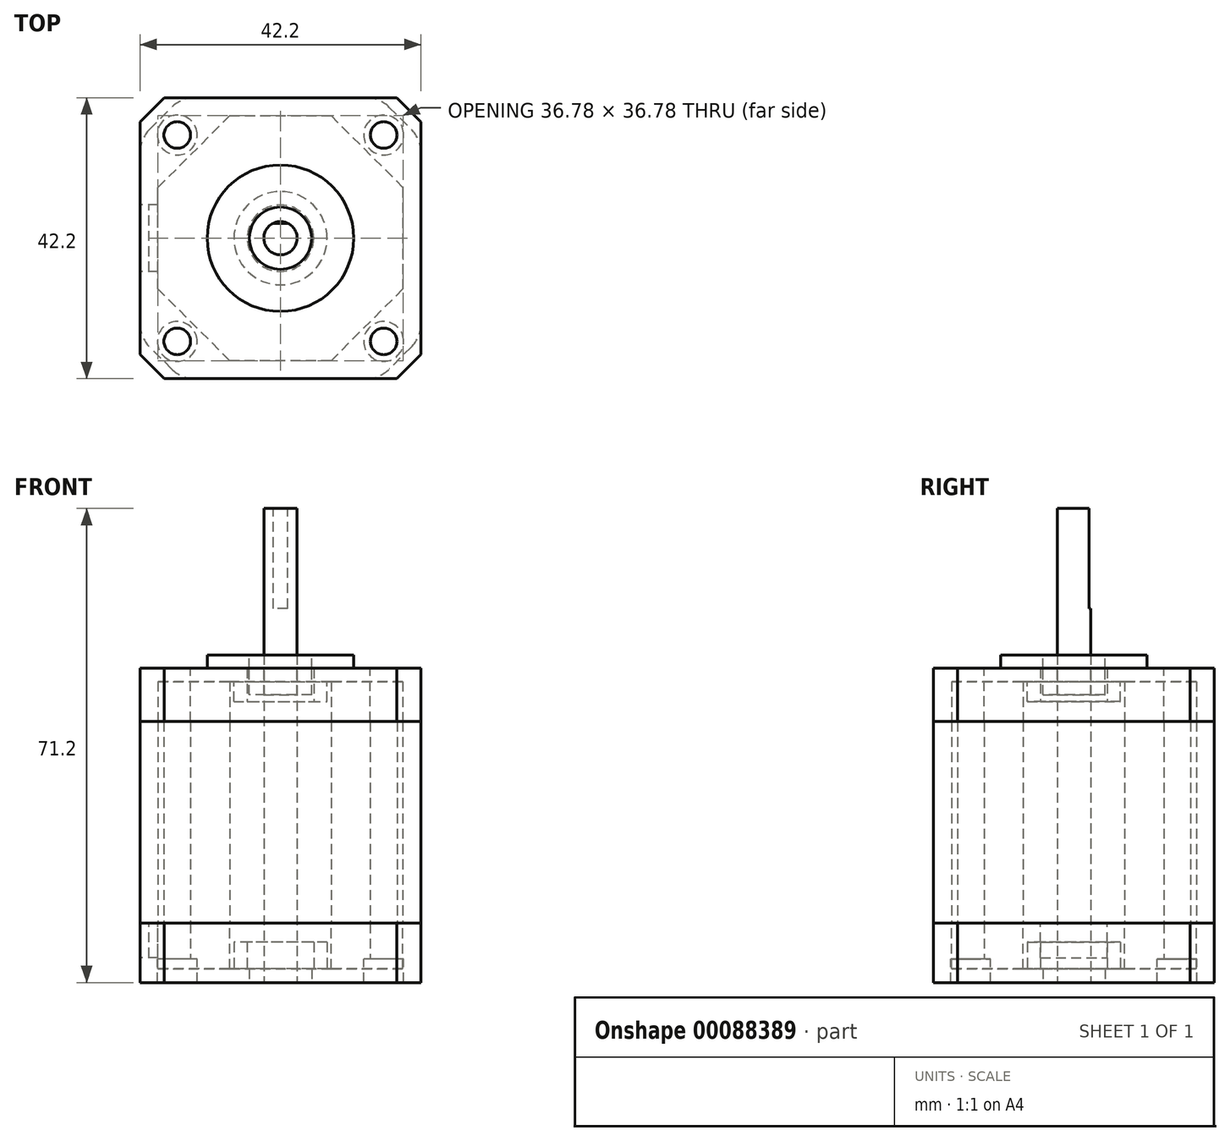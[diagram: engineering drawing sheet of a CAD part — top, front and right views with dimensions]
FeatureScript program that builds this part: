
annotation { "Feature Type Name" : "Feature", "Feature Type Description" : "" }
export const myFeature = defineFeature(function(context is Context, id is Id, definition is map)
    precondition{}
    {
        {
            var Q0;
            Q0=qCreatedBy(makeId("Top.planeOp"),FACE);
            var sketch = newSketch(context, id + "F0", { "sketchPlane" : qUnion([Q0])});
            skLineSegment(sketch, "E0.bottom", {"start": v(17.44, 21.1) * mm, "end": v(-17.44, 21.1) * mm});
            skLineSegment(sketch, "E0.top", {"start": v(17.44, -21.1) * mm, "end": v(-17.44, -21.1) * mm});
            skLineSegment(sketch, "E0.left", {"start": v(21.1, 17.44) * mm, "end": v(21.1, -17.44) * mm});
            skLineSegment(sketch, "E0.right", {"start": v(-21.1, 17.44) * mm, "end": v(-21.1, -17.44) * mm});
            skPoint(sketch, "E0.middle", {"position": v(0, 0) * mm});
            skLineSegment(sketch, "E1.bottom", {"start": v(15.5, 15.5) * mm, "end": v(-15.5, 15.5) * mm, "construction": true});
            skLineSegment(sketch, "E1.top", {"start": v(15.5, -15.5) * mm, "end": v(-15.5, -15.5) * mm, "construction": true});
            skLineSegment(sketch, "E1.left", {"start": v(15.5, 15.5) * mm, "end": v(15.5, -15.5) * mm, "construction": true});
            skLineSegment(sketch, "E1.right", {"start": v(-15.5, 15.5) * mm, "end": v(-15.5, -15.5) * mm, "construction": true});
            skCircle(sketch, "E2", {"center": v(-15.5, 15.5) * mm, "radius": 2 * mm});
            skCircle(sketch, "E3", {"center": v(15.5, 15.5) * mm, "radius": 2 * mm});
            skCircle(sketch, "E4", {"center": v(-15.5, -15.5) * mm, "radius": 2 * mm});
            skCircle(sketch, "E5", {"center": v(15.5, -15.5) * mm, "radius": 2 * mm});
            skLineSegment(sketch, "E6.1", {"start": v(-21.1, 17.44) * mm, "end": v(-17.44, 21.1) * mm});
            skLineSegment(sketch, "E7", {"start": v(0, 21.1) * mm, "end": v(0, -21.1) * mm, "construction": true});
            skLineSegment(sketch, "E8", {"start": v(-21.1, 0) * mm, "end": v(21.1, 0) * mm, "construction": true});
            skLineSegment(sketch, "E9.MirrorCS", {"start": v(21.1, 17.44) * mm, "end": v(17.44, 21.1) * mm});
            skLineSegment(sketch, "E10.MirrorCS", {"start": v(-21.1, -17.44) * mm, "end": v(-17.44, -21.1) * mm});
            skLineSegment(sketch, "E11.MirrorCS", {"start": v(21.1, -17.44) * mm, "end": v(17.44, -21.1) * mm});
            skCircle(sketch, "E12", {"center": v(0, 0) * mm, "radius": 4.68 * mm});
            skCircle(sketch, "E13", {"center": v(0, 0) * mm, "radius": 2.5 * mm});
            skCircle(sketch, "E14", {"center": v(0, 0) * mm, "radius": 11 * mm});
            skSolve(sketch);
        }
        {
            var Q0;
            Q0=makeQuery(id+"F0.imprint","IMPRINT",FACE,{"disambiguationData":[TD([[makeQuery(id+"F0.imprint","IMPRINT",EDGE,{"derivedFrom":sQuery(id+"F0.wireOp",EDGE,"E0.bottom")}),1.0]])]});
            var Q1;
            Q1=makeQuery(id+"F0.imprint","IMPRINT",FACE,{"disambiguationData":[TD([[makeQuery(id+"F0.imprint","IMPRINT",EDGE,{"derivedFrom":sQuery(id+"F0.wireOp",EDGE,"E12")}),-1.0]])]});
            extrude(context, id + "F1", {"entities" : qUnion([Q0, Q1]), "oppositeDirection" : true, "depth" : 8 * mm});
        }
        {
            var Q0;
            Q0=makeQuery(id+"F0.imprint","IMPRINT",FACE,{"disambiguationData":[TD([[makeQuery(id+"F0.imprint","IMPRINT",EDGE,{"derivedFrom":sQuery(id+"F0.wireOp",EDGE,"E12")}),-1.0]])]});
            extrude(context, id + "F2", {"entities" : qUnion([Q0]), "operationType" : NewBodyOperationType.ADD, "depth" : 2 * mm});
        }
        {
            var Q0;
            Q0=makeQuery(id+"F1.opExtrude","CAP_FACE",FACE,{"disambiguationData":[OSD([sQuery(id+"F0.wireOp",EDGE,"E0.bottom"),sQuery(id+"F0.wireOp",EDGE,"E0.top"),sQuery(id+"F0.wireOp",EDGE,"E0.left"),sQuery(id+"F0.wireOp",EDGE,"E0.right"),sQuery(id+"F0.wireOp",EDGE,"E2"),sQuery(id+"F0.wireOp",EDGE,"E3"),sQuery(id+"F0.wireOp",EDGE,"E4"),sQuery(id+"F0.wireOp",EDGE,"E5"),sQuery(id+"F0.wireOp",EDGE,"E6.1"),sQuery(id+"F0.wireOp",EDGE,"E9.MirrorCS"),sQuery(id+"F0.wireOp",EDGE,"E10.MirrorCS"),sQuery(id+"F0.wireOp",EDGE,"E11.MirrorCS"),sQuery(id+"F0.wireOp",EDGE,"E12")])],"isStart":true});
            cPlane(context, id + "F3", {"entities" : qUnion([Q0]), "cplaneType" : CPlaneType.OFFSET, "offset" : (47.2 - 3.5) * mm, "oppositeDirection" : true, "width" : 150 * mm, "height" : 150 * mm});
        }
        {
            var Q0;
            Q0=qCreatedBy(id+"F3.planeOp",FACE);
            var sketch = newSketch(context, id + "F4", { "sketchPlane" : qUnion([Q0])});
            skLineSegment(sketch, "E15.0", {"start": v(17.44, 21.1) * mm, "end": v(-17.44, 21.1) * mm});
            skLineSegment(sketch, "E15.1", {"start": v(17.44, -21.1) * mm, "end": v(-17.44, -21.1) * mm});
            skLineSegment(sketch, "E15.2", {"start": v(21.1, 17.44) * mm, "end": v(21.1, -17.44) * mm});
            skLineSegment(sketch, "E15.3", {"start": v(-21.1, 17.44) * mm, "end": v(-21.1, -17.44) * mm});
            skPoint(sketch, "E15.4", {"position": v(0, 0) * mm});
            skLineSegment(sketch, "E15.5", {"start": v(15.5, 15.5) * mm, "end": v(-15.5, 15.5) * mm, "construction": true});
            skLineSegment(sketch, "E15.6", {"start": v(15.5, -15.5) * mm, "end": v(-15.5, -15.5) * mm, "construction": true});
            skLineSegment(sketch, "E15.7", {"start": v(15.5, 15.5) * mm, "end": v(15.5, -15.5) * mm, "construction": true});
            skLineSegment(sketch, "E15.8", {"start": v(-15.5, 15.5) * mm, "end": v(-15.5, -15.5) * mm, "construction": true});
            skPoint(sketch, "E15.9", {"position": v(0, 0) * mm});
            skCircle(sketch, "E15.10", {"center": v(-15.5, 15.5) * mm, "radius": 2 * mm});
            skCircle(sketch, "E15.11", {"center": v(15.5, 15.5) * mm, "radius": 2 * mm});
            skCircle(sketch, "E15.12", {"center": v(-15.5, -15.5) * mm, "radius": 2 * mm});
            skCircle(sketch, "E15.13", {"center": v(15.5, -15.5) * mm, "radius": 2 * mm});
            skLineSegment(sketch, "E15.14", {"start": v(-21.1, 17.44) * mm, "end": v(-17.44, 21.1) * mm});
            skLineSegment(sketch, "E15.15", {"start": v(0, 21.1) * mm, "end": v(0, -21.1) * mm, "construction": true});
            skLineSegment(sketch, "E15.16", {"start": v(-21.1, 0) * mm, "end": v(21.1, 0) * mm, "construction": true});
            skLineSegment(sketch, "E15.17", {"start": v(21.1, 17.44) * mm, "end": v(17.44, 21.1) * mm});
            skLineSegment(sketch, "E15.18", {"start": v(-21.1, -17.44) * mm, "end": v(-17.44, -21.1) * mm});
            skLineSegment(sketch, "E15.19", {"start": v(21.1, -17.44) * mm, "end": v(17.44, -21.1) * mm});
            skCircle(sketch, "E15.20", {"center": v(0, 0) * mm, "radius": 4.68 * mm});
            skCircle(sketch, "E15.21", {"center": v(0, 0) * mm, "radius": 2.5 * mm});
            skCircle(sketch, "E16", {"center": v(15.5, 15.5) * mm, "radius": 3 * mm});
            skCircle(sketch, "E17.MirrorC", {"center": v(-15.5, 15.5) * mm, "radius": 3 * mm});
            skCircle(sketch, "E18.MirrorC", {"center": v(-15.5, -15.5) * mm, "radius": 3 * mm});
            skCircle(sketch, "E19.MirrorC", {"center": v(15.5, -15.5) * mm, "radius": 3 * mm});
            skSolve(sketch);
        }
        {
            var Q0;
            Q0=makeQuery(id+"F4.imprint","IMPRINT",FACE,{"disambiguationData":[TD([[makeQuery(id+"F4.imprint","IMPRINT",EDGE,{"derivedFrom":sQuery(id+"F4.wireOp",EDGE,"E15.0")}),1.0]])]});
            var Q1;
            Q1=makeQuery(id+"F4.imprint","IMPRINT",FACE,{"disambiguationData":[TD([[makeQuery(id+"F4.imprint","IMPRINT",EDGE,{"derivedFrom":sQuery(id+"F4.wireOp",EDGE,"E15.11")}),-1.0]])]});
            var Q2;
            Q2=makeQuery(id+"F4.imprint","IMPRINT",FACE,{"disambiguationData":[TD([[makeQuery(id+"F4.imprint","IMPRINT",EDGE,{"derivedFrom":sQuery(id+"F4.wireOp",EDGE,"E15.10")}),-1.0]])]});
            var Q3;
            Q3=makeQuery(id+"F4.imprint","IMPRINT",FACE,{"disambiguationData":[TD([[makeQuery(id+"F4.imprint","IMPRINT",EDGE,{"derivedFrom":sQuery(id+"F4.wireOp",EDGE,"E15.12")}),-1.0]])]});
            var Q4;
            Q4=makeQuery(id+"F4.imprint","IMPRINT",FACE,{"disambiguationData":[TD([[makeQuery(id+"F4.imprint","IMPRINT",EDGE,{"derivedFrom":sQuery(id+"F4.wireOp",EDGE,"E15.13")}),-1.0]])]});
            extrude(context, id + "F5", {"entities" : qUnion([Q0, Q1, Q2, Q3, Q4]), "depth" : (8.9 - 3.5) * mm});
        }
        {
            var Q0;
            Q0=makeQuery(id+"F4.imprint","IMPRINT",FACE,{"disambiguationData":[TD([[makeQuery(id+"F4.imprint","IMPRINT",EDGE,{"derivedFrom":sQuery(id+"F4.wireOp",EDGE,"E15.0")}),1.0]])]});
            extrude(context, id + "F6", {"entities" : qUnion([Q0]), "operationType" : NewBodyOperationType.ADD, "oppositeDirection" : true, "depth" : 3.5 * mm});
        }
        {
            var Q0;
            Q0=makeQuery(id+"F5.opExtrude","CAP_FACE",FACE,{"disambiguationData":[OSD([sQuery(id+"F4.wireOp",EDGE,"E15.0"),sQuery(id+"F4.wireOp",EDGE,"E15.1"),sQuery(id+"F4.wireOp",EDGE,"E15.2"),sQuery(id+"F4.wireOp",EDGE,"E15.3"),sQuery(id+"F4.wireOp",EDGE,"E15.10"),sQuery(id+"F4.wireOp",EDGE,"E15.11"),sQuery(id+"F4.wireOp",EDGE,"E15.12"),sQuery(id+"F4.wireOp",EDGE,"E15.13"),sQuery(id+"F4.wireOp",EDGE,"E15.14"),sQuery(id+"F4.wireOp",EDGE,"E15.17"),sQuery(id+"F4.wireOp",EDGE,"E15.18"),sQuery(id+"F4.wireOp",EDGE,"E15.19"),sQuery(id+"F4.wireOp",EDGE,"E15.20")])],"isStart":false});
            var sketch = newSketch(context, id + "F7", { "sketchPlane" : qUnion([Q0])});
            skLineSegment(sketch, "E20.1", {"start": v(16.7, -19.3) * mm, "end": v(19.3, -16.7) * mm});
            skLineSegment(sketch, "E20.2", {"start": v(19.3, 16.7) * mm, "end": v(16.7, 19.3) * mm});
            skLineSegment(sketch, "E20.5", {"start": v(-16.69, 19.3) * mm, "end": v(-19.3, 16.7) * mm});
            skLineSegment(sketch, "E20.7", {"start": v(-19.3, -16.7) * mm, "end": v(-16.7, -19.3) * mm});
            skLineSegment(sketch, "E21.0", {"start": v(-19.64, 16.36) * mm, "end": v(-19.3, 16.7) * mm});
            skLineSegment(sketch, "E21.2", {"start": v(16.36, 19.64) * mm, "end": v(16.7, 19.3) * mm});
            skLineSegment(sketch, "E21.4", {"start": v(19.64, -16.36) * mm, "end": v(19.3, -16.7) * mm});
            skLineSegment(sketch, "E21.6", {"start": v(-16.36, -19.64) * mm, "end": v(-19.64, -16.36) * mm});
            skLineSegment(sketch, "E22.0", {"start": v(-21.1, 12.82) * mm, "end": v(-21.1, -12.82) * mm});
            skLineSegment(sketch, "E22.1", {"start": v(-21.1, 17.44) * mm, "end": v(-17.44, 21.1) * mm});
            skLineSegment(sketch, "E22.2", {"start": v(12.82, 21.1) * mm, "end": v(-12.82, 21.1) * mm});
            skLineSegment(sketch, "E22.3", {"start": v(21.1, 17.44) * mm, "end": v(17.44, 21.1) * mm});
            skLineSegment(sketch, "E22.4", {"start": v(21.1, 12.82) * mm, "end": v(21.1, -12.82) * mm});
            skLineSegment(sketch, "E22.5", {"start": v(21.1, -17.44) * mm, "end": v(17.44, -21.1) * mm});
            skLineSegment(sketch, "E22.6", {"start": v(12.82, -21.1) * mm, "end": v(-12.82, -21.1) * mm});
            skLineSegment(sketch, "E22.7", {"start": v(-21.1, -17.44) * mm, "end": v(-17.44, -21.1) * mm});
            skPoint(sketch, "E23.orphan", {"position": v(-10.54, 25.45) * mm});
            skLineSegment(sketch, "E24.trimOffspring", {"start": v(16.7, -19.3) * mm, "end": v(16.36, -19.64) * mm});
            skLineSegment(sketch, "E25.trimOffspring", {"start": v(19.3, 16.7) * mm, "end": v(19.64, 16.36) * mm});
            skLineSegment(sketch, "E26.trimOffspring", {"start": v(-16.69, 19.3) * mm, "end": v(-16.36, 19.64) * mm});
            skCircle(sketch, "E27.cCircle", {"center": v(0, 0) * mm, "radius": 18.4 * mm, "construction": true});
            skLineSegment(sketch, "E27.0", {"start": v(-18.4, 7.61) * mm, "end": v(-7.62, 18.39) * mm});
            skLineSegment(sketch, "E27.1", {"start": v(-7.62, 18.39) * mm, "end": v(7.61, 18.4) * mm});
            skLineSegment(sketch, "E27.2", {"start": v(7.61, 18.4) * mm, "end": v(18.39, 7.62) * mm});
            skLineSegment(sketch, "E27.3", {"start": v(18.39, 7.62) * mm, "end": v(18.4, -7.61) * mm});
            skLineSegment(sketch, "E27.4", {"start": v(18.4, -7.61) * mm, "end": v(7.62, -18.39) * mm});
            skLineSegment(sketch, "E27.5", {"start": v(7.62, -18.39) * mm, "end": v(-7.61, -18.4) * mm});
            skLineSegment(sketch, "E27.6", {"start": v(-7.61, -18.4) * mm, "end": v(-18.39, -7.62) * mm});
            skLineSegment(sketch, "E27.7", {"start": v(-18.39, -7.62) * mm, "end": v(-18.4, 7.61) * mm});
            skLineSegment(sketch, "E28", {"start": v(0, 21.1) * mm, "end": v(0, -21.1) * mm, "construction": true});
            skPoint(sketch, "E29.newPointA", {"position": v(17.44, 21.1) * mm});
            skArc(sketch, "E29.filletArc", {"start": v(16.36, 19.64) * mm, "mid": v(14.73, 20.72) * mm, "end": v(12.82, 21.1) * mm});
            skArc(sketch, "E30.filletArc", {"start": v(21.1, 12.82) * mm, "mid": v(20.72, 14.73) * mm, "end": v(19.64, 16.36) * mm});
            skPoint(sketch, "E31.newPointB", {"position": v(-21.1, 17.44) * mm});
            skArc(sketch, "E31.filletArc", {"start": v(-19.64, 16.36) * mm, "mid": v(-20.72, 14.73) * mm, "end": v(-21.1, 12.82) * mm});
            skPoint(sketch, "E32.newPointB", {"position": v(-17.44, 21.1) * mm});
            skArc(sketch, "E32.filletArc", {"start": v(-12.82, 21.1) * mm, "mid": v(-14.73, 20.72) * mm, "end": v(-16.36, 19.64) * mm});
            skPoint(sketch, "E33.newPointB", {"position": v(21.1, -17.44) * mm});
            skArc(sketch, "E33.filletArc", {"start": v(19.64, -16.36) * mm, "mid": v(20.72, -14.73) * mm, "end": v(21.1, -12.82) * mm});
            skArc(sketch, "E34.filletArc", {"start": v(12.82, -21.1) * mm, "mid": v(14.73, -20.72) * mm, "end": v(16.36, -19.64) * mm});
            skPoint(sketch, "E35.newPointA", {"position": v(-21.1, -17.44) * mm});
            skArc(sketch, "E35.filletArc", {"start": v(-21.1, -12.82) * mm, "mid": v(-20.72, -14.73) * mm, "end": v(-19.64, -16.36) * mm});
            skPoint(sketch, "E36.newPointB", {"position": v(-17.44, -21.1) * mm});
            skArc(sketch, "E36.filletArc", {"start": v(-16.36, -19.64) * mm, "mid": v(-14.73, -20.72) * mm, "end": v(-12.82, -21.1) * mm});
            skPoint(sketch, "E37.middle", {"position": v(-18.4, 0) * mm});
            skSolve(sketch);
        }
        {
            var Q0;
            Q0=makeQuery(id+"F7.imprint","IMPRINT",FACE,{"disambiguationData":[TD([[makeQuery(id+"F7.imprint","IMPRINT",EDGE,{"derivedFrom":sQuery(id+"F7.wireOp",EDGE,"E20.1")}),1.0]])]});
            extrude(context, id + "F8", {"entities" : qUnion([Q0]), "endBound" : BoundingType.UP_TO_NEXT, "depth" : 25 * mm});
        }
        {
            var Q0;
            Q0=makeQuery(id+"F0.imprint","IMPRINT",FACE,{"disambiguationData":[TD([[makeQuery(id+"F0.imprint","IMPRINT",EDGE,{"derivedFrom":sQuery(id+"F0.wireOp",EDGE,"E13")}),1.0]])]});
            extrude(context, id + "F9", {"entities" : qUnion([Q0]), "depth" : 24 * mm});
        }
        {
            var Q0;
            Q0=makeQuery(id+"F0.imprint","IMPRINT",FACE,{"disambiguationData":[TD([[makeQuery(id+"F0.imprint","IMPRINT",EDGE,{"derivedFrom":sQuery(id+"F0.wireOp",EDGE,"E13")}),1.0]])]});
            var Q1;
            Q1=makeQuery(id+"F6.opExtrude","CAP_FACE",FACE,{"disambiguationData":[OSD([sQuery(id+"F4.wireOp",EDGE,"E15.0"),sQuery(id+"F4.wireOp",EDGE,"E15.1"),sQuery(id+"F4.wireOp",EDGE,"E15.2"),sQuery(id+"F4.wireOp",EDGE,"E15.3"),sQuery(id+"F4.wireOp",EDGE,"E15.14"),sQuery(id+"F4.wireOp",EDGE,"E15.17"),sQuery(id+"F4.wireOp",EDGE,"E15.18"),sQuery(id+"F4.wireOp",EDGE,"E15.19"),sQuery(id+"F4.wireOp",EDGE,"E15.20"),sQuery(id+"F4.wireOp",EDGE,"E16"),sQuery(id+"F4.wireOp",EDGE,"E17.MirrorC"),sQuery(id+"F4.wireOp",EDGE,"E18.MirrorC"),sQuery(id+"F4.wireOp",EDGE,"E19.MirrorC")])],"isStart":false});
            extrude(context, id + "F10", {"entities" : qUnion([Q0]), "operationType" : NewBodyOperationType.ADD, "endBound" : BoundingType.UP_TO_SURFACE, "oppositeDirection" : true, "endBoundEntityFace" : qUnion([Q1]), "depth" : 25 * mm});
        }
        {
            var Q0;
            Q0=makeQuery(id+"F9.opExtrude","CAP_FACE",FACE,{"disambiguationData":[OSD([sQuery(id+"F0.wireOp",EDGE,"E13")])],"isStart":false});
            var sketch = newSketch(context, id + "F11", { "sketchPlane" : qUnion([Q0])});
            skLineSegment(sketch, "E38", {"start": v(0, 0) * mm, "end": v(0, 2.25) * mm, "construction": true});
            skLineSegment(sketch, "E39", {"start": v(0, 2.25) * mm, "end": v(-1.09, 2.25) * mm});
            skLineSegment(sketch, "E40.MirrorCS", {"start": v(0, 2.25) * mm, "end": v(1.09, 2.25) * mm});
            skCircle(sketch, "E41.0", {"center": v(0, 0) * mm, "radius": 2.5 * mm});
            skSolve(sketch);
        }
        {
            var Q0;
            {var subQ0=sQuery(id+"F11.wireOp",EDGE,"E39");Q0=makeQuery(id+"F11.imprint","IMPRINT",FACE,{"disambiguationData":[TD([[makeQuery(id+"F11.imprint","IMPRINT",EDGE,{"derivedFrom":subQ0}),-1.0]])]});}
            extrude(context, id + "F12", {"entities" : qUnion([Q0]), "operationType" : NewBodyOperationType.REMOVE, "oppositeDirection" : true, "depth" : 15 * mm});
        }
        {
            var Q0;
            Q0=makeQuery(id+"F7.imprint","IMPRINT",FACE,{"disambiguationData":[TD([[makeQuery(id+"F7.imprint","IMPRINT",EDGE,{"derivedFrom":sQuery(id+"F7.wireOp",EDGE,"E27.0")}),-1.0]])]});
            extrude(context, id + "F13", {"entities" : qUnion([Q0]), "operationType" : NewBodyOperationType.REMOVE, "oppositeDirection" : true, "depth" : (8.86 - 2) * mm});
        }
        {
            var Q0;
            Q0=makeQuery(id+"F1.opExtrude","CAP_FACE",FACE,{"disambiguationData":[OSD([sQuery(id+"F0.wireOp",EDGE,"E0.bottom"),sQuery(id+"F0.wireOp",EDGE,"E0.top"),sQuery(id+"F0.wireOp",EDGE,"E0.left"),sQuery(id+"F0.wireOp",EDGE,"E0.right"),sQuery(id+"F0.wireOp",EDGE,"E2"),sQuery(id+"F0.wireOp",EDGE,"E3"),sQuery(id+"F0.wireOp",EDGE,"E4"),sQuery(id+"F0.wireOp",EDGE,"E5"),sQuery(id+"F0.wireOp",EDGE,"E6.1"),sQuery(id+"F0.wireOp",EDGE,"E9.MirrorCS"),sQuery(id+"F0.wireOp",EDGE,"E10.MirrorCS"),sQuery(id+"F0.wireOp",EDGE,"E11.MirrorCS"),sQuery(id+"F0.wireOp",EDGE,"E12")])],"isStart":false});
            var sketch = newSketch(context, id + "F14", { "sketchPlane" : qUnion([Q0])});
            skLineSegment(sketch, "E42.0.0", {"start": v(-7.62, -18.39) * mm, "end": v(-18.4, -7.61) * mm});
            skLineSegment(sketch, "E42.0.1", {"start": v(-18.4, -7.61) * mm, "end": v(-18.39, 7.62) * mm});
            skLineSegment(sketch, "E42.0.2", {"start": v(-18.39, 7.62) * mm, "end": v(-7.61, 18.4) * mm});
            skLineSegment(sketch, "E42.0.3", {"start": v(-7.61, 18.4) * mm, "end": v(7.62, 18.39) * mm});
            skLineSegment(sketch, "E42.0.4", {"start": v(7.62, 18.39) * mm, "end": v(18.4, 7.61) * mm});
            skLineSegment(sketch, "E42.0.5", {"start": v(18.4, 7.61) * mm, "end": v(18.39, -7.62) * mm});
            skLineSegment(sketch, "E42.0.6", {"start": v(18.39, -7.62) * mm, "end": v(7.61, -18.4) * mm});
            skLineSegment(sketch, "E42.0.7", {"start": v(7.61, -18.4) * mm, "end": v(-7.62, -18.39) * mm});
            skSolve(sketch);
        }
        {
            var Q0;
            Q0=makeQuery(id+"F14.imprint","IMPRINT",FACE,{"disambiguationData":[TD([[makeQuery(id+"F14.imprint","IMPRINT",EDGE,{"derivedFrom":sQuery(id+"F14.wireOp",EDGE,"E42.0.0")}),-1.0]])]});
            extrude(context, id + "F15", {"entities" : qUnion([Q0]), "operationType" : NewBodyOperationType.REMOVE, "oppositeDirection" : true, "depth" : 6 * mm});
        }
        {
            var Q0;
            Q0=makeQuery(id+"F15.boolean.opBoolean","COPY",FACE,{"derivedFrom":makeQuery(id+"F15.opExtrude","CAP_FACE",FACE,{"disambiguationData":[OSD([sQuery(id+"F0.wireOp",EDGE,"E12"),sQuery(id+"F14.wireOp",EDGE,"E42.0.0"),sQuery(id+"F14.wireOp",EDGE,"E42.0.1"),sQuery(id+"F14.wireOp",EDGE,"E42.0.2"),sQuery(id+"F14.wireOp",EDGE,"E42.0.3"),sQuery(id+"F14.wireOp",EDGE,"E42.0.4"),sQuery(id+"F14.wireOp",EDGE,"E42.0.5"),sQuery(id+"F14.wireOp",EDGE,"E42.0.6"),sQuery(id+"F14.wireOp",EDGE,"E42.0.7")])],"isStart":false})});
            var sketch = newSketch(context, id + "F16", { "sketchPlane" : qUnion([Q0])});
            skCircle(sketch, "E43.0", {"center": v(0, 0) * mm, "radius": 4.68 * mm});
            skCircle(sketch, "E44", {"center": v(0, 0) * mm, "radius": 5 * mm});
            skCircle(sketch, "E45", {"center": v(0, 0) * mm, "radius": 7 * mm});
            skSolve(sketch);
        }
        {
            var Q0;
            Q0=makeQuery(id+"F16.imprint","IMPRINT",FACE,{"disambiguationData":[TD([[makeQuery(id+"F16.imprint","IMPRINT",EDGE,{"derivedFrom":sQuery(id+"F16.wireOp",EDGE,"E43.0")}),1.0]])]});
            extrude(context, id + "F17", {"entities" : qUnion([Q0]), "operationType" : NewBodyOperationType.REMOVE, "oppositeDirection" : true, "depth" : 2 * mm});
        }
        {
            var Q0;
            Q0=makeQuery(id+"F16.imprint","IMPRINT",FACE,{"disambiguationData":[TD([[makeQuery(id+"F16.imprint","IMPRINT",EDGE,{"derivedFrom":sQuery(id+"F16.wireOp",EDGE,"E44")}),-1.0]])]});
            var Q1;
            Q1=makeQuery(id+"F1.opExtrude","CAP_FACE",FACE,{"disambiguationData":[OSD([sQuery(id+"F0.wireOp",EDGE,"E0.bottom"),sQuery(id+"F0.wireOp",EDGE,"E0.top"),sQuery(id+"F0.wireOp",EDGE,"E0.left"),sQuery(id+"F0.wireOp",EDGE,"E0.right"),sQuery(id+"F0.wireOp",EDGE,"E2"),sQuery(id+"F0.wireOp",EDGE,"E3"),sQuery(id+"F0.wireOp",EDGE,"E4"),sQuery(id+"F0.wireOp",EDGE,"E5"),sQuery(id+"F0.wireOp",EDGE,"E6.1"),sQuery(id+"F0.wireOp",EDGE,"E9.MirrorCS"),sQuery(id+"F0.wireOp",EDGE,"E10.MirrorCS"),sQuery(id+"F0.wireOp",EDGE,"E11.MirrorCS"),sQuery(id+"F0.wireOp",EDGE,"E12")])],"isStart":false});
            extrude(context, id + "F18", {"entities" : qUnion([Q0]), "operationType" : NewBodyOperationType.ADD, "endBoundEntityFace" : qUnion([Q1]), "depth" : 3 * mm});
        }
        {
            var Q0;
            Q0=makeQuery(id+"F13.boolean.opBoolean","COPY",FACE,{"derivedFrom":makeQuery(id+"F13.opExtrude","CAP_FACE",FACE,{"disambiguationData":[OSD([sQuery(id+"F4.wireOp",EDGE,"E15.20"),sQuery(id+"F7.wireOp",EDGE,"E27.0"),sQuery(id+"F7.wireOp",EDGE,"E27.1"),sQuery(id+"F7.wireOp",EDGE,"E27.2"),sQuery(id+"F7.wireOp",EDGE,"E27.3"),sQuery(id+"F7.wireOp",EDGE,"E27.4"),sQuery(id+"F7.wireOp",EDGE,"E27.5"),sQuery(id+"F7.wireOp",EDGE,"E27.6"),sQuery(id+"F7.wireOp",EDGE,"E27.7")])],"isStart":false})});
            var sketch = newSketch(context, id + "F19", { "sketchPlane" : qUnion([Q0])});
            skCircle(sketch, "E46.0.0", {"center": v(0, 0) * mm, "radius": 7 * mm});
            skCircle(sketch, "E47.0", {"center": v(0, 0) * mm, "radius": 4.68 * mm});
            skCircle(sketch, "E47.1", {"center": v(0, 0) * mm, "radius": 5 * mm});
            skSolve(sketch);
        }
        {
            var Q0;
            Q0=makeQuery(id+"F19.imprint","IMPRINT",FACE,{"disambiguationData":[TD([[makeQuery(id+"F19.imprint","IMPRINT",EDGE,{"derivedFrom":sQuery(id+"F19.wireOp",EDGE,"E46.0.0")}),1.0]])]});
            var Q1;
            Q1=makeQuery(id+"F5.opExtrude","CAP_FACE",FACE,{"disambiguationData":[OSD([sQuery(id+"F4.wireOp",EDGE,"E15.0"),sQuery(id+"F4.wireOp",EDGE,"E15.1"),sQuery(id+"F4.wireOp",EDGE,"E15.2"),sQuery(id+"F4.wireOp",EDGE,"E15.3"),sQuery(id+"F4.wireOp",EDGE,"E15.10"),sQuery(id+"F4.wireOp",EDGE,"E15.11"),sQuery(id+"F4.wireOp",EDGE,"E15.12"),sQuery(id+"F4.wireOp",EDGE,"E15.13"),sQuery(id+"F4.wireOp",EDGE,"E15.14"),sQuery(id+"F4.wireOp",EDGE,"E15.17"),sQuery(id+"F4.wireOp",EDGE,"E15.18"),sQuery(id+"F4.wireOp",EDGE,"E15.19"),sQuery(id+"F4.wireOp",EDGE,"E15.20")])],"isStart":false});
            extrude(context, id + "F20", {"entities" : qUnion([Q0]), "operationType" : NewBodyOperationType.ADD, "endBoundEntityFace" : qUnion([Q1]), "depth" : 4 * mm});
        }
        {
            var Q0;
            Q0=makeQuery(id+"F17.boolean.opBoolean","COPY",FACE,{"derivedFrom":makeQuery(id+"F17.opExtrude","CAP_FACE",FACE,{"disambiguationData":[OSD([sQuery(id+"F16.wireOp",EDGE,"E43.0"),sQuery(id+"F16.wireOp",EDGE,"E44")])],"isStart":false})});
            var sketch = newSketch(context, id + "F21", { "sketchPlane" : qUnion([Q0])});
            skCircle(sketch, "E48", {"center": v(0, 0) * mm, "radius": 2.5 * mm});
            skCircle(sketch, "E49", {"center": v(0, 0) * mm, "radius": 5 * mm});
            skSolve(sketch);
        }
        {
            var Q0;
            Q0=makeQuery(id+"F21.imprint","IMPRINT",FACE,{"disambiguationData":[TD([[makeQuery(id+"F21.imprint","IMPRINT",EDGE,{"derivedFrom":sQuery(id+"F21.wireOp",EDGE,"E48")}),-1.0]])]});
            extrude(context, id + "F22", {"entities" : qUnion([Q0]), "depth" : 4 * mm});
        }
        {
            var Q0;
            {var subQ0=sQuery(id+"F4.wireOp",EDGE,"E15.3");Q0=makeQuery(id+"F6.boolean.opBoolean","MERGE",FACE,{"derivedFrom":[makeQuery(id+"F5.opExtrude","SWEPT_FACE",FACE,{"disambiguationData":[OSD([subQ0])]}),makeQuery(id+"F6.opExtrude","SWEPT_FACE",FACE,{"disambiguationData":[OSD([subQ0])]})]});}
            var sketch = newSketch(context, id + "F23", { "sketchPlane" : qUnion([Q0])});
            skLineSegment(sketch, "E50.bottom", {"start": v(5, -43.46) * mm, "end": v(-5, -43.46) * mm});
            skLineSegment(sketch, "E50.left", {"start": v(5, -43.46) * mm, "end": v(5, -38.3) * mm});
            skLineSegment(sketch, "E50.right", {"start": v(-5, -43.46) * mm, "end": v(-5, -38.3) * mm});
            skPoint(sketch, "E50.middle", {"position": v(0, -38.3) * mm});
            skSolve(sketch);
        }
        {
            var Q0;
            Q0=makeQuery(id+"F23.imprint","IMPRINT",FACE,{"disambiguationData":[TD([[makeQuery(id+"F23.imprint","IMPRINT",EDGE,{"derivedFrom":sQuery(id+"F23.wireOp",EDGE,"E50.bottom")}),-1.0]])]});
            extrude(context, id + "F24", {"entities" : qUnion([Q0]), "operationType" : NewBodyOperationType.REMOVE, "endBound" : BoundingType.UP_TO_NEXT, "oppositeDirection" : true, "depth" : 25 * mm});
        }
        {
            var Q0;
            Q0=makeQuery(id+"F24.boolean.opBoolean","COPY",FACE,{"derivedFrom":makeQuery(id+"F24.opExtrude","SWEPT_FACE",FACE,{"disambiguationData":[OSD([sQuery(id+"F23.wireOp",EDGE,"E50.right")])]})});
            var sketch = newSketch(context, id + "F25", { "sketchPlane" : qUnion([Q0])});
            skLineSegment(sketch, "E51.bottom", {"start": v(-18.4, -43.46) * mm, "end": v(-19.75, -43.46) * mm});
            skLineSegment(sketch, "E51.top", {"start": v(-18.4, -38.3) * mm, "end": v(-19.75, -38.3) * mm});
            skLineSegment(sketch, "E51.left", {"start": v(-18.4, -43.46) * mm, "end": v(-18.4, -38.3) * mm});
            skLineSegment(sketch, "E51.right", {"start": v(-19.75, -43.46) * mm, "end": v(-19.75, -38.3) * mm});
            skSolve(sketch);
        }
        {
            var Q0;
            Q0=makeQuery(id+"F25.imprint","IMPRINT",FACE,{"disambiguationData":[TD([[makeQuery(id+"F25.imprint","IMPRINT",EDGE,{"derivedFrom":sQuery(id+"F25.wireOp",EDGE,"E51.bottom")}),-1.0]])]});
            var Q1;
            Q1=makeQuery(id+"F24.boolean.opBoolean","COPY",FACE,{"derivedFrom":makeQuery(id+"F24.opExtrude","SWEPT_FACE",FACE,{"disambiguationData":[OSD([sQuery(id+"F23.wireOp",EDGE,"E50.left")])]})});
            extrude(context, id + "F26", {"entities" : qUnion([Q0]), "endBound" : BoundingType.UP_TO_SURFACE, "endBoundEntityFace" : qUnion([Q1]), "depth" : 25 * mm});
        }
    });
